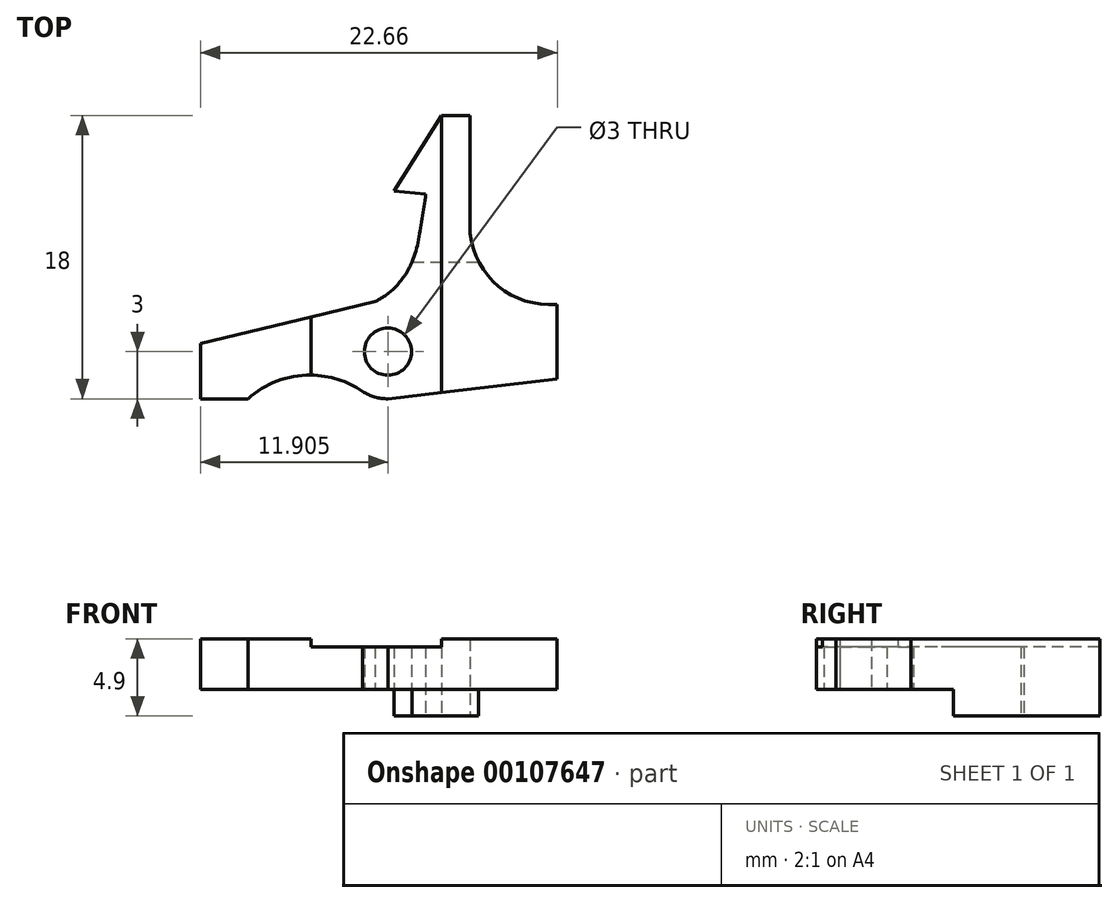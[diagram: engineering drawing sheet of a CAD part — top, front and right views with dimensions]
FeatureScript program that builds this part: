
annotation { "Feature Type Name" : "Feature", "Feature Type Description" : "" }
export const myFeature = defineFeature(function(context is Context, id is Id, definition is map)
    precondition{}
    {
        {
            var Q0;
            Q0=qCreatedBy(makeId("Top.planeOp"),FACE);
            var sketch = newSketch(context, id + "F0", { "sketchPlane" : qUnion([Q0])});
            skLineSegment(sketch, "E0.bottom", {"start": v(-11.32, -3) * mm, "end": v(-8.32, -3) * mm});
            skLineSegment(sketch, "E0.top", {"start": v(10.77, 3) * mm, "end": v(11.31, 3) * mm});
            skLineSegment(sketch, "E0.left", {"start": v(-11.32, -3) * mm, "end": v(-11.32, 0.5) * mm});
            skPoint(sketch, "E0.middle", {"position": v(0, 0) * mm});
            skCircle(sketch, "E1", {"center": v(0.58, 0) * mm, "radius": 1.5 * mm});
            skArc(sketch, "E2", {"start": v(-1.15, -2.45) * mm, "mid": v(-0.33, -2.86) * mm, "end": v(0.58, -3) * mm});
            skArc(sketch, "E3", {"start": v(-1.04, -2.53) * mm, "mid": v(-4.76, -1.5) * mm, "end": v(-8.32, -3) * mm});
            skLineSegment(sketch, "E4", {"start": v(3.97, 15) * mm, "end": v(3.97, 4.7) * mm});
            skLineSegment(sketch, "E5", {"start": v(5.77, 15) * mm, "end": v(5.77, 8) * mm});
            skLineSegment(sketch, "E6", {"start": v(-11.33, 0.5) * mm, "end": v(-0.24, 3.17) * mm});
            skLineSegment(sketch, "E7", {"start": v(3.97, 15) * mm, "end": v(5.77, 15) * mm});
            skLineSegment(sketch, "E8", {"start": v(3.97, 15) * mm, "end": v(0.97, 10.18) * mm});
            skFitSpline(sketch, "E9", {"points": [v(2.97, 10) * mm, v(2.6, 7.57) * mm, v(2, 5.46) * mm, v(0.8, 3.86) * mm, v(-0.24, 3.17) * mm], "startDerivative": vector(-1.24, -8.8) * mm, "endDerivative": vector(-5.15, -2.87) * mm});
            skPoint(sketch, "E10.orphan", {"position": v(0, 1.39) * mm});
            skArc(sketch, "E11.filletArc", {"start": v(5.77, 8) * mm, "mid": v(6.1, 6.23) * mm, "end": v(7.02, 4.7) * mm});
            skLineSegment(sketch, "E12", {"start": v(-4.32, 2.19) * mm, "end": v(-4.32, -1.5) * mm});
            skLineSegment(sketch, "E13", {"start": v(2.11, 5.7) * mm, "end": v(6.34, 5.7) * mm});
            skLineSegment(sketch, "E14", {"start": v(1.55, 4.7) * mm, "end": v(3.97, 4.7) * mm});
            skPoint(sketch, "E15.orphan", {"position": v(11.32, 3) * mm});
            skLineSegment(sketch, "E16", {"start": v(11.32, -1.75) * mm, "end": v(11.32, -1.75) * mm});
            skLineSegment(sketch, "E17", {"start": v(11.32, -1.75) * mm, "end": v(11.32, 3) * mm});
            skLineSegment(sketch, "E18", {"start": v(11.32, 3) * mm, "end": v(11.32, 3) * mm});
            skLineSegment(sketch, "E19", {"start": v(3.98, -2.6) * mm, "end": v(3.98, -2.6) * mm});
            skLineSegment(sketch, "E20", {"start": v(3.98, -2.6) * mm, "end": v(0.57, -3) * mm});
            skLineSegment(sketch, "E21", {"start": v(3.98, -2.6) * mm, "end": v(11.32, -1.75) * mm});
            skLineSegment(sketch, "E22", {"start": v(2.97, 10) * mm, "end": v(0.97, 10.18) * mm});
            skLineSegment(sketch, "E23", {"start": v(3.97, 4.7) * mm, "end": v(3.98, -2.6) * mm});
            skArc(sketch, "E24", {"start": v(7.02, 4.7) * mm, "mid": v(8.72, 3.44) * mm, "end": v(10.77, 3) * mm});
            skLineSegment(sketch, "E25", {"start": v(3.97, 4.7) * mm, "end": v(7.02, 4.7) * mm});
            skLineSegment(sketch, "E26", {"start": v(11.32, 3) * mm, "end": v(10.77, 3) * mm});
            skSolve(sketch);
        }
        {
            var Q0;
            Q0=makeQuery(id+"F0.imprint","IMPRINT",FACE,{"disambiguationData":[TD([[makeQuery(id+"F0.imprint","IMPRINT",EDGE,{"derivedFrom":sQuery(id+"F0.wireOp",EDGE,"E1")}),-1.0]])]});
            extrude(context, id + "F1", {"entities" : qUnion([Q0]), "depth" : 2.7 * mm});
        }
        {
            var Q0;
            {var subQ4=sQuery(id+"F0.wireOp",EDGE,"E0.bottom");Q0=makeQuery(id+"F0.imprint","IMPRINT",FACE,{"disambiguationData":[TD([[makeQuery(id+"F0.imprint","IMPRINT",EDGE,{"derivedFrom":subQ4}),1.0]])]});}
            extrude(context, id + "F2", {"entities" : qUnion([Q0]), "operationType" : NewBodyOperationType.ADD, "depth" : 3.2 * mm});
        }
        {
            var Q0;
            {var subQ0=sQuery(id+"F0.wireOp",EDGE,"E13");var subQ1=sQuery(id+"F0.wireOp",EDGE,"E4");var subQ2=makeQuery(id+"F0.imprint","INTERSECT",VERTEX,{"derivedFrom":[subQ1,subQ0]});Q0=makeQuery(id+"F0.imprint","IMPRINT",FACE,{"disambiguationData":[TD([[makeQuery(id+"F0.imprint","IMPRINT",EDGE,{"disambiguationData":[TD([[subQ2,-1.0]])],"derivedFrom":subQ1}),-1.0]])]});}
            var Q1;
            {var subQ6=sQuery(id+"F0.wireOp",EDGE,"E8");Q1=makeQuery(id+"F0.imprint","IMPRINT",FACE,{"disambiguationData":[TD([[makeQuery(id+"F0.imprint","IMPRINT",EDGE,{"derivedFrom":subQ6}),1.0]])]});}
            extrude(context, id + "F3", {"entities" : qUnion([Q0, Q1]), "operationType" : NewBodyOperationType.ADD, "depth" : 2.7 * mm});
        }
        {
            var Q0;
            {var subQ1=sQuery(id+"F0.wireOp",EDGE,"E5");Q0=makeQuery(id+"F0.imprint","IMPRINT",FACE,{"disambiguationData":[TD([[makeQuery(id+"F0.imprint","IMPRINT",EDGE,{"derivedFrom":subQ1}),-1.0]])]});}
            var Q1;
            {var subQ0=sQuery(id+"F0.wireOp",EDGE,"E13");var subQ1=sQuery(id+"F0.wireOp",EDGE,"E4");var subQ2=makeQuery(id+"F0.imprint","INTERSECT",VERTEX,{"derivedFrom":[subQ1,subQ0]});Q1=makeQuery(id+"F0.imprint","IMPRINT",FACE,{"disambiguationData":[TD([[makeQuery(id+"F0.imprint","IMPRINT",EDGE,{"disambiguationData":[TD([[subQ2,-1.0]])],"derivedFrom":subQ1}),1.0]])]});}
            var Q2;
            {var subQ6=sQuery(id+"F0.wireOp",EDGE,"E0.top");Q2=makeQuery(id+"F0.imprint","IMPRINT",FACE,{"disambiguationData":[TD([[makeQuery(id+"F0.imprint","IMPRINT",EDGE,{"derivedFrom":subQ6}),-1.0]])]});}
            extrude(context, id + "F4", {"entities" : qUnion([Q0, Q1, Q2]), "operationType" : NewBodyOperationType.ADD, "depth" : 3.2 * mm});
        }
        {
            var Q0;
            {var subQ1=sQuery(id+"F0.wireOp",EDGE,"E5");Q0=makeQuery(id+"F0.imprint","IMPRINT",FACE,{"disambiguationData":[TD([[makeQuery(id+"F0.imprint","IMPRINT",EDGE,{"derivedFrom":subQ1}),-1.0]])]});}
            var Q1;
            {var subQ6=sQuery(id+"F0.wireOp",EDGE,"E8");Q1=makeQuery(id+"F0.imprint","IMPRINT",FACE,{"disambiguationData":[TD([[makeQuery(id+"F0.imprint","IMPRINT",EDGE,{"derivedFrom":subQ6}),1.0]])]});}
            extrude(context, id + "F5", {"entities" : qUnion([Q0, Q1]), "operationType" : NewBodyOperationType.ADD, "oppositeDirection" : true, "depth" : 1.7 * mm});
        }
        {
            var Q0;
            Q0=makeQuery(id+"F0.imprint","IMPRINT",FACE,{"disambiguationData":[TD([[makeQuery(id+"F0.imprint","IMPRINT",EDGE,{"derivedFrom":sQuery(id+"F0.wireOp",EDGE,"E17")}),1.0]])]});
            extrude(context, id + "F6", {"entities" : qUnion([Q0]), "operationType" : NewBodyOperationType.ADD, "depth" : 3.2 * mm});
        }
    });
